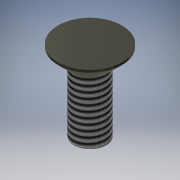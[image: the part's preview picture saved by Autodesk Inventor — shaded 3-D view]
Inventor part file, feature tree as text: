
AUTODESK INVENTOR PART (.ipt)
format: ipt  version: 2016 (Build 200138000, 138)  size: 128,512 bytes
history: native  units: mm
features: extrude x3, sketch x3, other x1, thread x1, chamfer x1
ambient origin geometry x1: Origin
bodies: Body1 (feature_tree)
feature tree (9):
  other  "ソリッド1"
  extrude  "押し出し1"  Depth=4.0mm
  extrude  "押し出し2"  Depth=6.0mm TaperAngle=0.0deg
  thread  "ねじ1"
  chamfer  "面取り1"  Distance=8.0mm
  extrude  "押し出し4"  Depth=2.3mm TaperAngle=0.0deg
  sketch  "スケッチ1"
  sketch  "スケッチ2"
  sketch  "スケッチ4"
